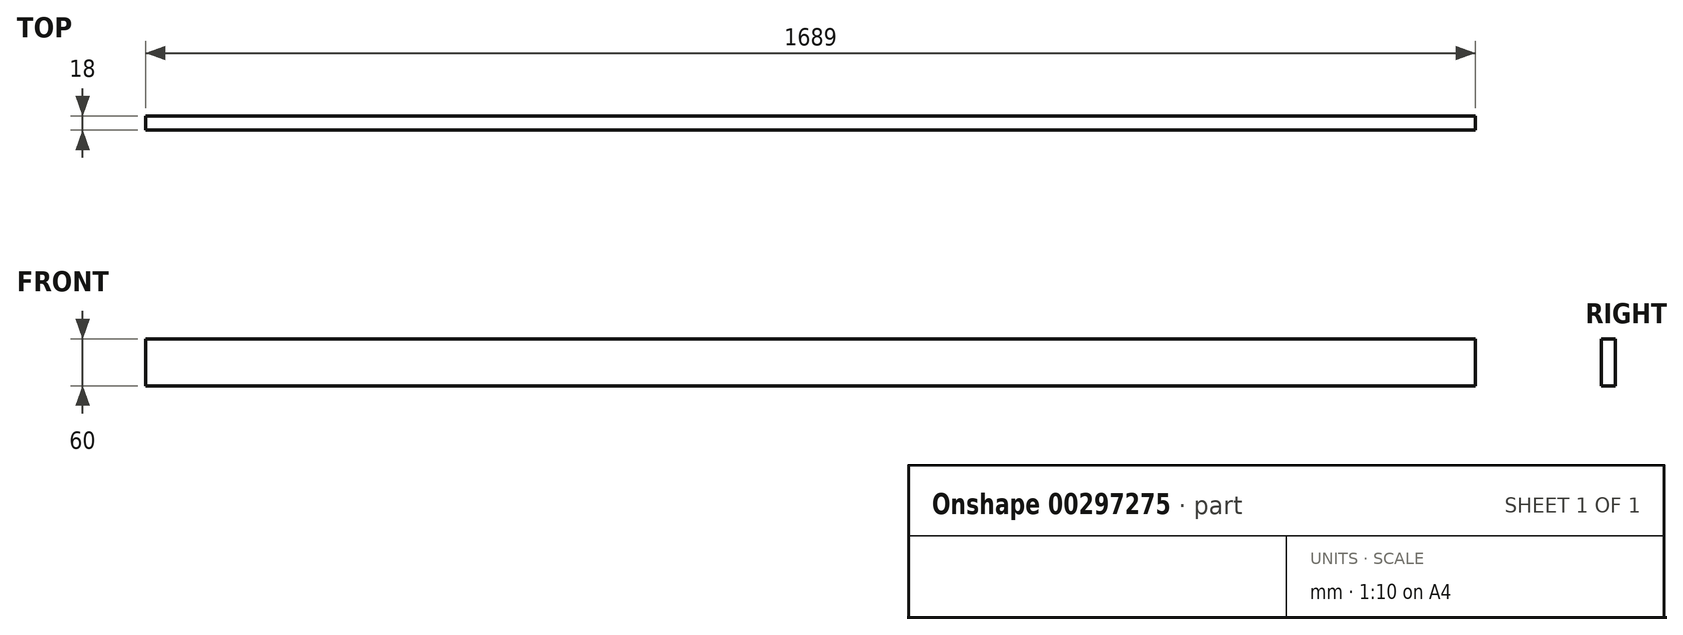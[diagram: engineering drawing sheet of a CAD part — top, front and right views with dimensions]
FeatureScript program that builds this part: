
annotation { "Feature Type Name" : "Feature", "Feature Type Description" : "" }
export const myFeature = defineFeature(function(context is Context, id is Id, definition is map)
    precondition{}
    {
        {
            var Q0;
            Q0=qCreatedBy(makeId("Right.planeOp"),FACE);
            var sketch = newSketch(context, id + "F0", { "sketchPlane" : qUnion([Q0])});
            skLineSegment(sketch, "E0.bottom", {"start": v(9, 30) * mm, "end": v(-9, 30) * mm});
            skLineSegment(sketch, "E0.top", {"start": v(9, -30) * mm, "end": v(-9, -30) * mm});
            skLineSegment(sketch, "E0.left", {"start": v(9, 30) * mm, "end": v(9, -30) * mm});
            skLineSegment(sketch, "E0.right", {"start": v(-9, 30) * mm, "end": v(-9, -30) * mm});
            skPoint(sketch, "E0.middle", {"position": v(0, 0) * mm});
            skSolve(sketch);
        }
        {
            var Q0;
            Q0 = qSketchRegion(id + "F0", true);
            extrude(context, id + "F1", {"entities" : qUnion([Q0]), "depth" : 1689 * mm});
        }
    });
